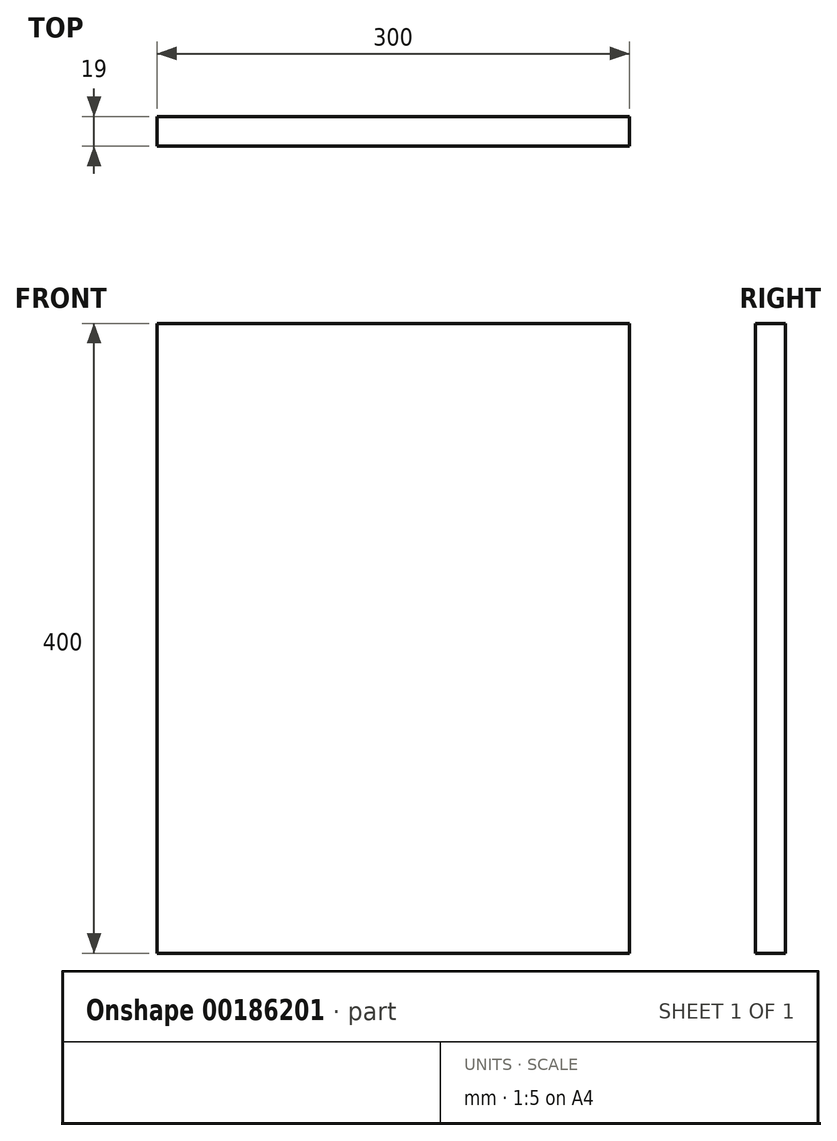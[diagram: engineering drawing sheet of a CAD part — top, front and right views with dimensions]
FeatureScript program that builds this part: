
annotation { "Feature Type Name" : "Feature", "Feature Type Description" : "" }
export const myFeature = defineFeature(function(context is Context, id is Id, definition is map)
    precondition{}
    {
        {
            var Q0;
            Q0=qCreatedBy(makeId("Front.planeOp"),FACE);
            var sketch = newSketch(context, id + "F0", { "sketchPlane" : qUnion([Q0])});
            skLineSegment(sketch, "E0.bottom", {"start": v(-113.56, 228.54) * mm, "end": v(186.44, 228.54) * mm});
            skLineSegment(sketch, "E0.top", {"start": v(-113.56, -171.46) * mm, "end": v(186.44, -171.46) * mm});
            skLineSegment(sketch, "E0.left", {"start": v(-113.56, 228.54) * mm, "end": v(-113.56, -171.46) * mm});
            skLineSegment(sketch, "E0.right", {"start": v(186.44, 228.54) * mm, "end": v(186.44, -171.46) * mm});
            skSolve(sketch);
        }
        {
            var Q0;
            Q0 = qSketchRegion(id + "F0", true);
            extrude(context, id + "F1", {"entities" : qUnion([Q0]), "depth" : 19 * mm});
        }
    });
